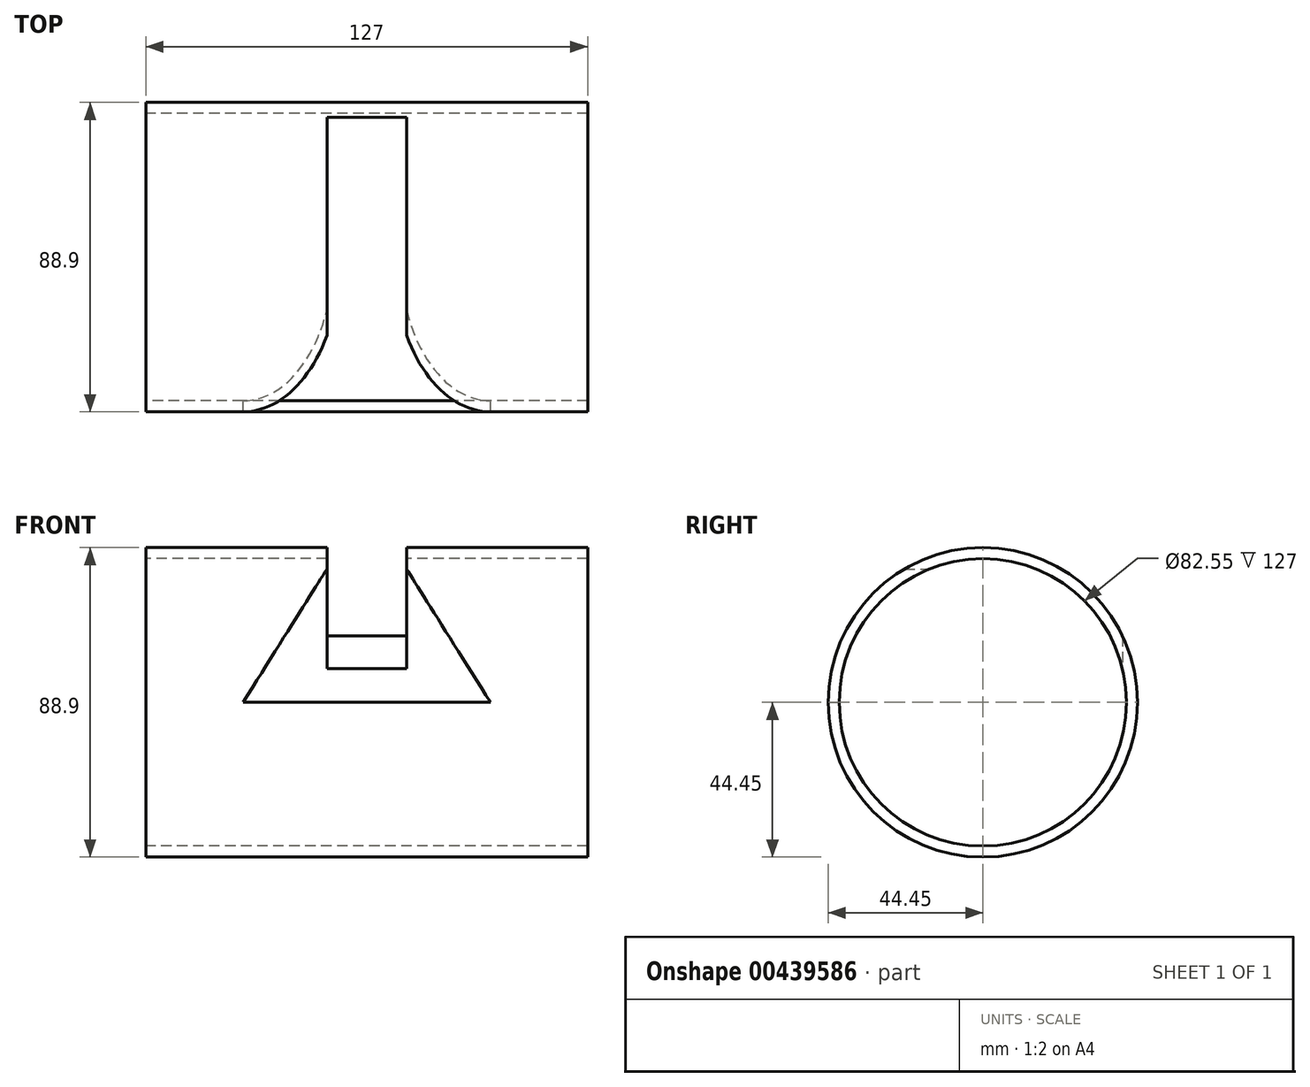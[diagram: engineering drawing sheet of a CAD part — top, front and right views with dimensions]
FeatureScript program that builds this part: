
annotation { "Feature Type Name" : "Feature", "Feature Type Description" : "" }
export const myFeature = defineFeature(function(context is Context, id is Id, definition is map)
    precondition{}
    {
        {
            var Q0;
            Q0=qCreatedBy(makeId("Right.planeOp"),FACE);
            var sketch = newSketch(context, id + "F0", { "sketchPlane" : qUnion([Q0])});
            skCircle(sketch, "E0", {"center": v(0, 0) * mm, "radius": 44.45 * mm});
            skCircle(sketch, "E1", {"center": v(0, 0) * mm, "radius": 41.28 * mm});
            skSolve(sketch);
        }
        {
            var Q0;
            Q0=makeQuery(id+"F0.imprint","IMPRINT",FACE,{"disambiguationData":[TD([[makeQuery(id+"F0.imprint","IMPRINT",EDGE,{"derivedFrom":sQuery(id+"F0.wireOp",EDGE,"E0")}),1.0]])]});
            extrude(context, id + "F1", {"entities" : qUnion([Q0]), "depth" : 63.5 * mm, "hasSecondDirection" : true, "secondDirectionOppositeDirection" : true, "secondDirectionDepth" : 63.5 * mm});
        }
        {
            var Q0;
            Q0=qCreatedBy(makeId("Front.planeOp"),FACE);
            var sketch = newSketch(context, id + "F2", { "sketchPlane" : qUnion([Q0])});
            skLineSegment(sketch, "E2", {"start": v(0, 0) * mm, "end": v(35.56, 0) * mm});
            skLineSegment(sketch, "E3", {"start": v(0, 0) * mm, "end": v(-35.56, 0) * mm});
            skLineSegment(sketch, "E4", {"start": v(0, 38.34) * mm, "end": v(-11.43, 38.34) * mm});
            skLineSegment(sketch, "E5", {"start": v(-35.56, 0) * mm, "end": v(-11.43, 38.34) * mm});
            skLineSegment(sketch, "E6", {"start": v(0, 38.34) * mm, "end": v(11.43, 38.34) * mm});
            skLineSegment(sketch, "E7", {"start": v(11.43, 38.34) * mm, "end": v(35.56, 0) * mm});
            skSolve(sketch);
        }
        {
            var Q0;
            Q0=makeQuery(id+"F2.imprint","IMPRINT",FACE,{"disambiguationData":[TD([[makeQuery(id+"F2.imprint","IMPRINT",EDGE,{"derivedFrom":sQuery(id+"F2.wireOp",EDGE,"E2")}),1.0]])]});
            extrude(context, id + "F3", {"entities" : qUnion([Q0]), "operationType" : NewBodyOperationType.REMOVE, "depth" : 57.9 * mm});
        }
        {
            var Q0;
            Q0=qCreatedBy(makeId("Top.planeOp"),FACE);
            var sketch = newSketch(context, id + "F4", { "sketchPlane" : qUnion([Q0])});
            skLineSegment(sketch, "E8", {"start": v(0, -23.69) * mm, "end": v(11.43, -23.69) * mm});
            skLineSegment(sketch, "E9", {"start": v(0, -23.69) * mm, "end": v(-11.43, -23.69) * mm});
            skLineSegment(sketch, "E10", {"start": v(-11.43, 27.4) * mm, "end": v(11.43, 27.4) * mm});
            skLineSegment(sketch, "E11", {"start": v(-11.43, 27.4) * mm, "end": v(-11.43, -23.69) * mm});
            skLineSegment(sketch, "E12", {"start": v(11.43, 27.4) * mm, "end": v(11.43, -23.69) * mm});
            skSolve(sketch);
        }
        {
            var Q0;
            Q0=makeQuery(id+"F4.imprint","IMPRINT",FACE,{"disambiguationData":[TD([[makeQuery(id+"F4.imprint","IMPRINT",EDGE,{"derivedFrom":sQuery(id+"F4.wireOp",EDGE,"E8")}),1.0]])]});
            extrude(context, id + "F5", {"entities" : qUnion([Q0]), "operationType" : NewBodyOperationType.REMOVE, "depth" : 91.7 * mm});
        }
        {
            var Q0;
            Q0=qCreatedBy(makeId("Front.planeOp"),FACE);
            var sketch = newSketch(context, id + "F6", { "sketchPlane" : qUnion([Q0])});
            skLineSegment(sketch, "E13", {"start": v(0, 0) * mm, "end": v(-11.43, 0) * mm});
            skLineSegment(sketch, "E14", {"start": v(0, 0) * mm, "end": v(11.43, 0) * mm});
            skLineSegment(sketch, "E15", {"start": v(0, 35.25) * mm, "end": v(11.43, 35.25) * mm});
            skLineSegment(sketch, "E16", {"start": v(11.43, 35.25) * mm, "end": v(11.43, 0) * mm});
            skLineSegment(sketch, "E17", {"start": v(0, 35.25) * mm, "end": v(-11.43, 35.25) * mm});
            skLineSegment(sketch, "E18", {"start": v(-11.43, 35.25) * mm, "end": v(-11.43, 0) * mm});
            skSolve(sketch);
        }
        {
            var Q0;
            Q0=makeQuery(id+"F6.imprint","IMPRINT",FACE,{"disambiguationData":[TD([[makeQuery(id+"F6.imprint","IMPRINT",EDGE,{"derivedFrom":sQuery(id+"F6.wireOp",EDGE,"E13")}),-1.0]])]});
            extrude(context, id + "F7", {"entities" : qUnion([Q0]), "operationType" : NewBodyOperationType.REMOVE, "oppositeDirection" : true, "depth" : 40.13 * mm});
        }
    });
